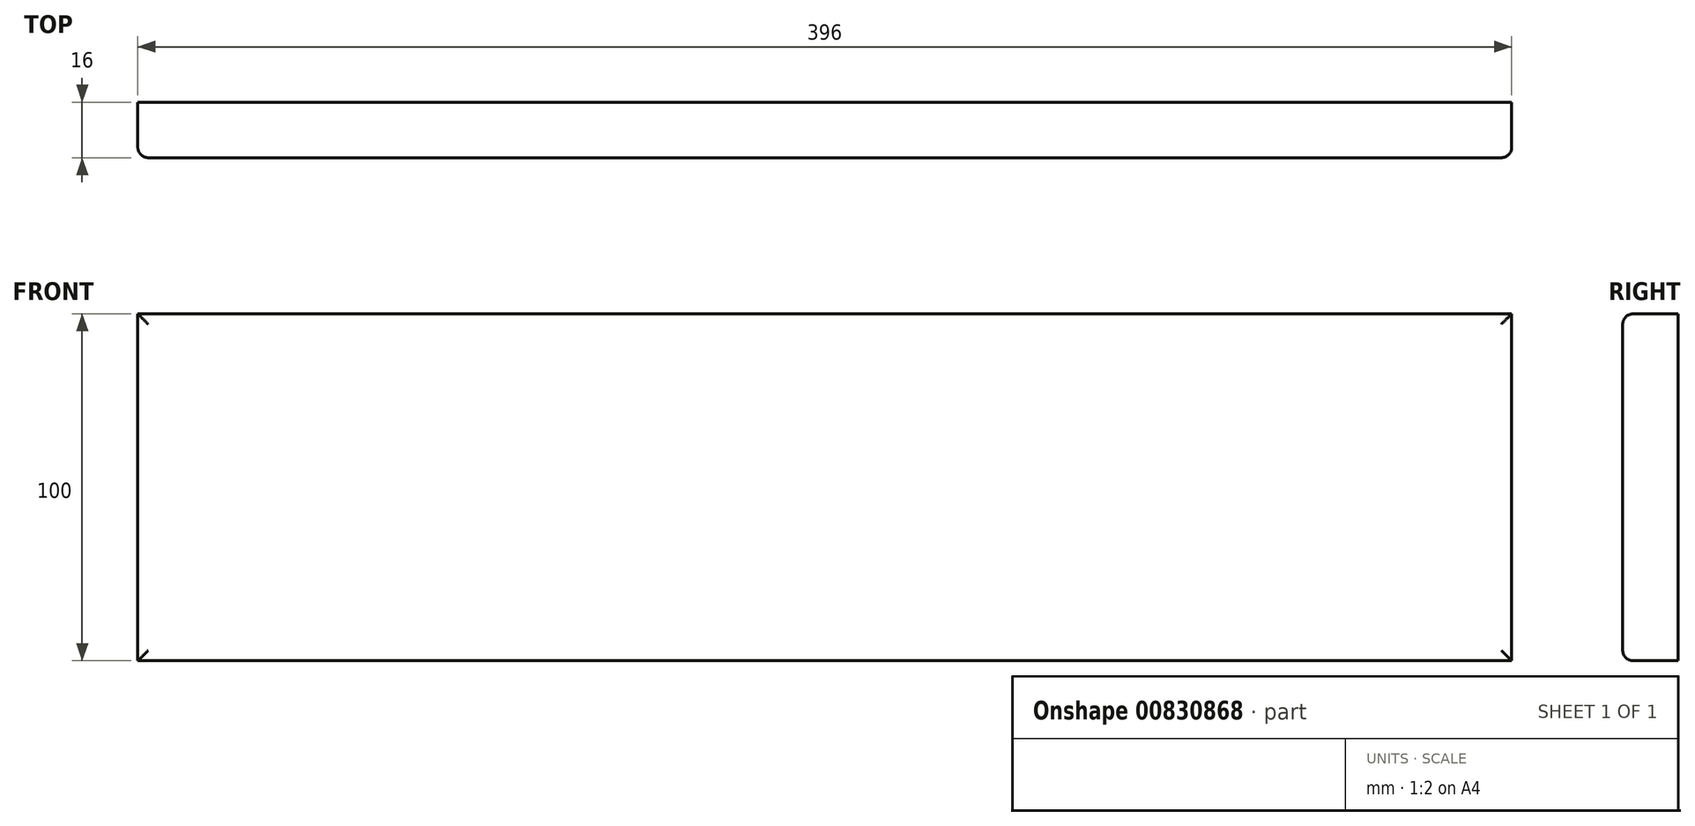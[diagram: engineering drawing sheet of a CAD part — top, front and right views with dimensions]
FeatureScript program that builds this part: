
annotation { "Feature Type Name" : "Feature", "Feature Type Description" : "" }
export const myFeature = defineFeature(function(context is Context, id is Id, definition is map)
    precondition{}
    {
        {
            var Q0;
            Q0=qCreatedBy(makeId("Front.planeOp"),FACE);
            var sketch = newSketch(context, id + "F0", { "sketchPlane" : qUnion([Q0])});
            skLineSegment(sketch, "E0.bottom", {"start": v(0, 0) * mm, "end": v(53.67, 0) * mm});
            skLineSegment(sketch, "E0.top", {"start": v(0, 36.38) * mm, "end": v(53.67, 36.38) * mm});
            skLineSegment(sketch, "E0.left", {"start": v(0, 0) * mm, "end": v(0, 36.38) * mm});
            skLineSegment(sketch, "E0.right", {"start": v(53.67, 0) * mm, "end": v(53.67, 36.38) * mm});
            skSolve(sketch);
        }
        {
            var Q0;
            Q0=makeQuery(id+"F0.imprint","IMPRINT",FACE,{"disambiguationData":[TD([[makeQuery(id+"F0.imprint","IMPRINT",EDGE,{"derivedFrom":sQuery(id+"F0.wireOp",EDGE,"E0.bottom")}),1.0]])]});
            extrude(context, id + "F1", {"entities" : qUnion([Q0]), "depth" : 16 * mm, "offsetDistance" : 25.4 * mm});
        }
        {
            var Q0;
            Q0=makeQuery(id+"F1.opExtrude","SWEPT_FACE",FACE,{"disambiguationData":[OSD([sQuery(id+"F0.wireOp",EDGE,"E0.left")])]});
            extrude(context, id + "F2", {"entities" : qUnion([Q0]), "operationType" : NewBodyOperationType.ADD, "oppositeDirection" : true, "depth" : 396 * mm, "offsetDistance" : 25 * mm});
        }
        {
            var Q0;
            {var subQ0=sQuery(id+"F0.wireOp",EDGE,"E0.bottom");Q0=makeQuery(id+"F2.boolean.opBoolean","MERGE",FACE,{"derivedFrom":[makeQuery(id+"F1.opExtrude","SWEPT_FACE",FACE,{"disambiguationData":[OSD([subQ0])]}),makeQuery(id+"F2.opExtrude","SWEPT_FACE",FACE,{"disambiguationData":[OSD([subQ0,sQuery(id+"F0.wireOp",EDGE,"E0.left")])]})]});}
            extrude(context, id + "F3", {"entities" : qUnion([Q0]), "operationType" : NewBodyOperationType.ADD, "oppositeDirection" : true, "depth" : 100 * mm, "offsetDistance" : 25 * mm});
        }
        {
            var Q0;
            {var subQ0=sQuery(id+"F0.wireOp",EDGE,"E0.left");var subQ1=sQuery(id+"F0.wireOp",EDGE,"E0.bottom");Q0=makeQuery(id+"F3.boolean.opBoolean","MERGE",FACE,{"derivedFrom":[makeQuery(id+"F2.boolean.opBoolean","MERGE",FACE,{"derivedFrom":[makeQuery(id+"F1.opExtrude","CAP_FACE",FACE,{"disambiguationData":[OSD([subQ1,sQuery(id+"F0.wireOp",EDGE,"E0.top"),subQ0,sQuery(id+"F0.wireOp",EDGE,"E0.right")])],"isStart":false}),makeQuery(id+"F2.opExtrude","SWEPT_FACE",FACE,{"disambiguationData":[OSD([subQ0]),TDD([makeQuery(id+"F1.opExtrude","CAP_EDGE",EDGE,{"disambiguationData":[OSD([subQ0])],"isStart":false})])]})]}),makeQuery(id+"F3.opExtrude","SWEPT_FACE",FACE,{"disambiguationData":[OSD([subQ1,subQ0]),TDD([makeQuery(id+"F2.boolean.opBoolean","MERGE",EDGE,{"derivedFrom":[makeQuery(id+"F1.opExtrude","CAP_EDGE",EDGE,{"disambiguationData":[OSD([subQ1])],"isStart":false}),makeQuery(id+"F2.opExtrude","SWEPT_EDGE",EDGE,{"disambiguationData":[OSD([subQ1,subQ0]),TDD([makeQuery(id+"F1.opExtrude","CAP_VERTEX",VERTEX,{"disambiguationData":[OSD([subQ1,subQ0])],"isStart":false})])]})]})])]})]});}
            fillet(context, id + "F4", {"entities" : qUnion([Q0]), "radius" : 3 * mm, "tangentPropagation" : true, "allowEdgeOverflow" : false});
        }
    });
